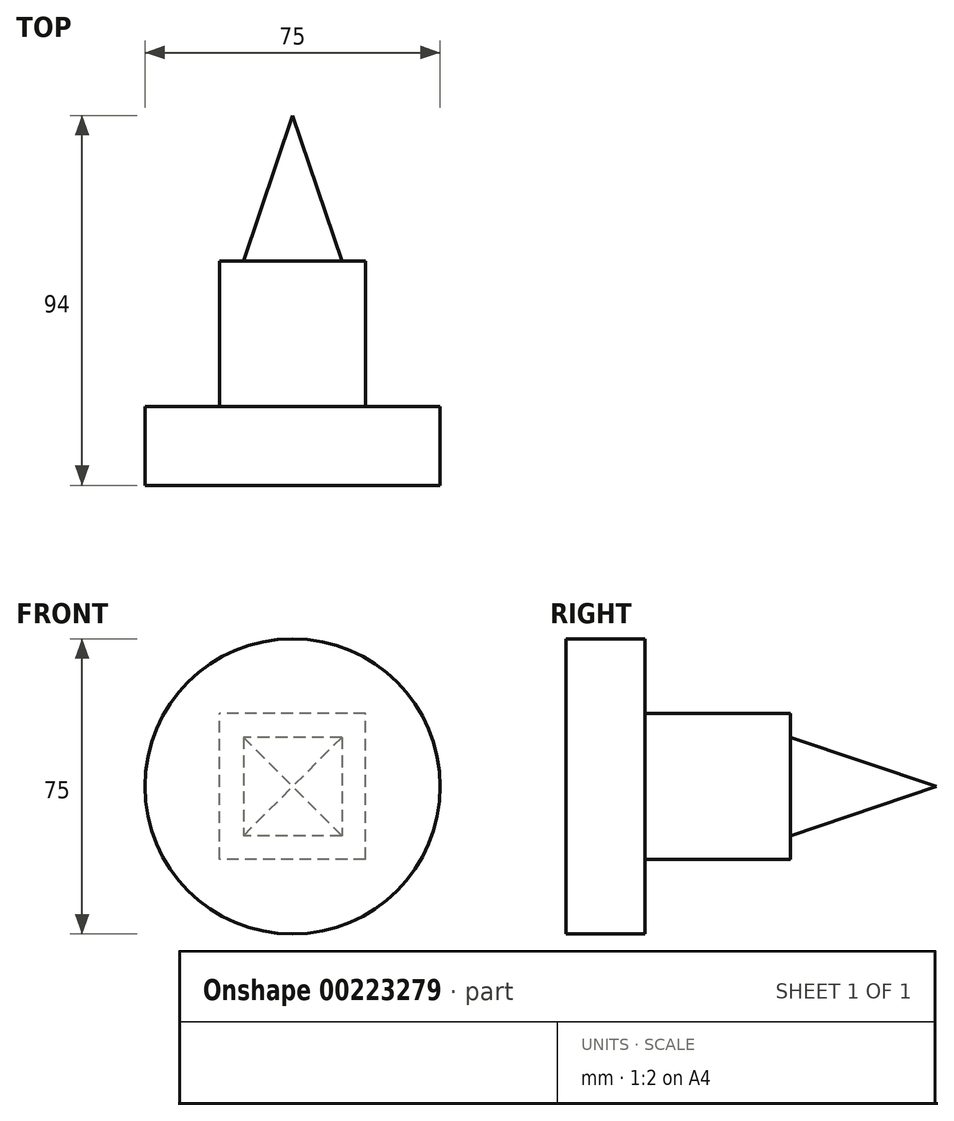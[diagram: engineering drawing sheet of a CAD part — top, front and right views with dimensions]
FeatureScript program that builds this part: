
annotation { "Feature Type Name" : "Feature", "Feature Type Description" : "" }
export const myFeature = defineFeature(function(context is Context, id is Id, definition is map)
    precondition{}
    {
        {
            var Q0;
            Q0=qCreatedBy(makeId("Front.planeOp"),FACE);
            var sketch = newSketch(context, id + "F0", { "sketchPlane" : qUnion([Q0])});
            skCircle(sketch, "E0", {"center": v(0, 0) * mm, "radius": 37.5 * mm});
            skSolve(sketch);
        }
        {
            var Q0;
            Q0 = qSketchRegion(id + "F0", true);
            extrude(context, id + "F1", {"entities" : qUnion([Q0]), "oppositeDirection" : true, "depth" : 20 * mm});
        }
        {
            var Q0;
            Q0=makeQuery(id+"F1.opExtrude","CAP_FACE",FACE,{"disambiguationData":[OSD([sQuery(id+"F0.wireOp",EDGE,"E0")])],"isStart":false});
            var sketch = newSketch(context, id + "F2", { "sketchPlane" : qUnion([Q0])});
            skLineSegment(sketch, "E1.bottom", {"start": v(-18.5, -18.5) * mm, "end": v(18.5, -18.5) * mm});
            skLineSegment(sketch, "E1.top", {"start": v(-18.5, 18.5) * mm, "end": v(18.5, 18.5) * mm});
            skLineSegment(sketch, "E1.left", {"start": v(-18.5, -18.5) * mm, "end": v(-18.5, 18.5) * mm});
            skLineSegment(sketch, "E1.right", {"start": v(18.5, -18.5) * mm, "end": v(18.5, 18.5) * mm});
            skPoint(sketch, "E1.middle", {"position": v(0, 0) * mm});
            skSolve(sketch);
        }
        {
            var Q0;
            Q0=makeQuery(id+"F2.imprint","IMPRINT",FACE,{"disambiguationData":[TD([[makeQuery(id+"F2.imprint","IMPRINT",EDGE,{"derivedFrom":sQuery(id+"F2.wireOp",EDGE,"E1.bottom")}),1.0]])]});
            extrude(context, id + "F3", {"entities" : qUnion([Q0]), "operationType" : NewBodyOperationType.ADD, "depth" : 37 * mm});
        }
        {
            var Q0;
            Q0=makeQuery(id+"F3.opExtrude","CAP_FACE",FACE,{"disambiguationData":[OSD([sQuery(id+"F2.wireOp",EDGE,"E1.bottom"),sQuery(id+"F2.wireOp",EDGE,"E1.top"),sQuery(id+"F2.wireOp",EDGE,"E1.left"),sQuery(id+"F2.wireOp",EDGE,"E1.right")])],"isStart":false});
            var sketch = newSketch(context, id + "F4", { "sketchPlane" : qUnion([Q0])});
            skLineSegment(sketch, "E2.bottom", {"start": v(-12.5, 12.5) * mm, "end": v(12.5, 12.5) * mm});
            skLineSegment(sketch, "E2.top", {"start": v(-12.5, -12.5) * mm, "end": v(12.5, -12.5) * mm});
            skLineSegment(sketch, "E2.left", {"start": v(-12.5, 12.5) * mm, "end": v(-12.5, -12.5) * mm});
            skLineSegment(sketch, "E2.right", {"start": v(12.5, 12.5) * mm, "end": v(12.5, -12.5) * mm});
            skPoint(sketch, "E2.middle", {"position": v(0, 0) * mm});
            skSolve(sketch);
        }
        {
            var Q0;
            Q0=makeQuery(id+"F4.imprint","IMPRINT",FACE,{"disambiguationData":[TD([[makeQuery(id+"F4.imprint","IMPRINT",EDGE,{"derivedFrom":sQuery(id+"F4.wireOp",EDGE,"E2.bottom")}),-1.0]])]});
            var sketch = newSketch(context, id + "F5", { "sketchPlane" : qUnion([Q0])});
            skSolve(sketch);
        }
        {
            var Q0;
            Q0=makeQuery(id+"F5.imprint","IMPRINT",FACE,{"disambiguationData":[TD([[makeQuery(id+"F5.imprint","IMPRINT",EDGE,{"derivedFrom":makeQuery(id+"F4.imprint","IMPRINT",EDGE,{"derivedFrom":sQuery(id+"F4.wireOp",EDGE,"E2.bottom")})}),-1.0]])]});
            cPlane(context, id + "F6", {"entities" : qUnion([Q0]), "cplaneType" : CPlaneType.OFFSET, "offset" : 37 * mm, "width" : 150 * mm, "height" : 150 * mm});
        }
        {
            var Q0;
            Q0=qCreatedBy(id+"F6.planeOp",FACE);
            var sketch = newSketch(context, id + "F7", { "sketchPlane" : qUnion([Q0])});
            skPoint(sketch, "E3", {"position": v(0, 0) * mm});
            skSolve(sketch);
        }
        {
            var Q1;
            Q1=makeQuery(id+"F4.imprint","IMPRINT",FACE,{"disambiguationData":[TD([[makeQuery(id+"F4.imprint","IMPRINT",EDGE,{"derivedFrom":sQuery(id+"F4.wireOp",EDGE,"E2.bottom")}),-1.0]])]});
            var Q2;
            Q2=sQuery(id+"F7.wireOp",VERTEX,"E3");
            loft(context, id + "F8", {"operationType" : NewBodyOperationType.ADD, "sheetProfilesArray" : [{ "sheetProfileEntities" : qUnion([Q1]) }, { "sheetProfileEntities" : qUnion([Q2]) }]});
        }
    });
